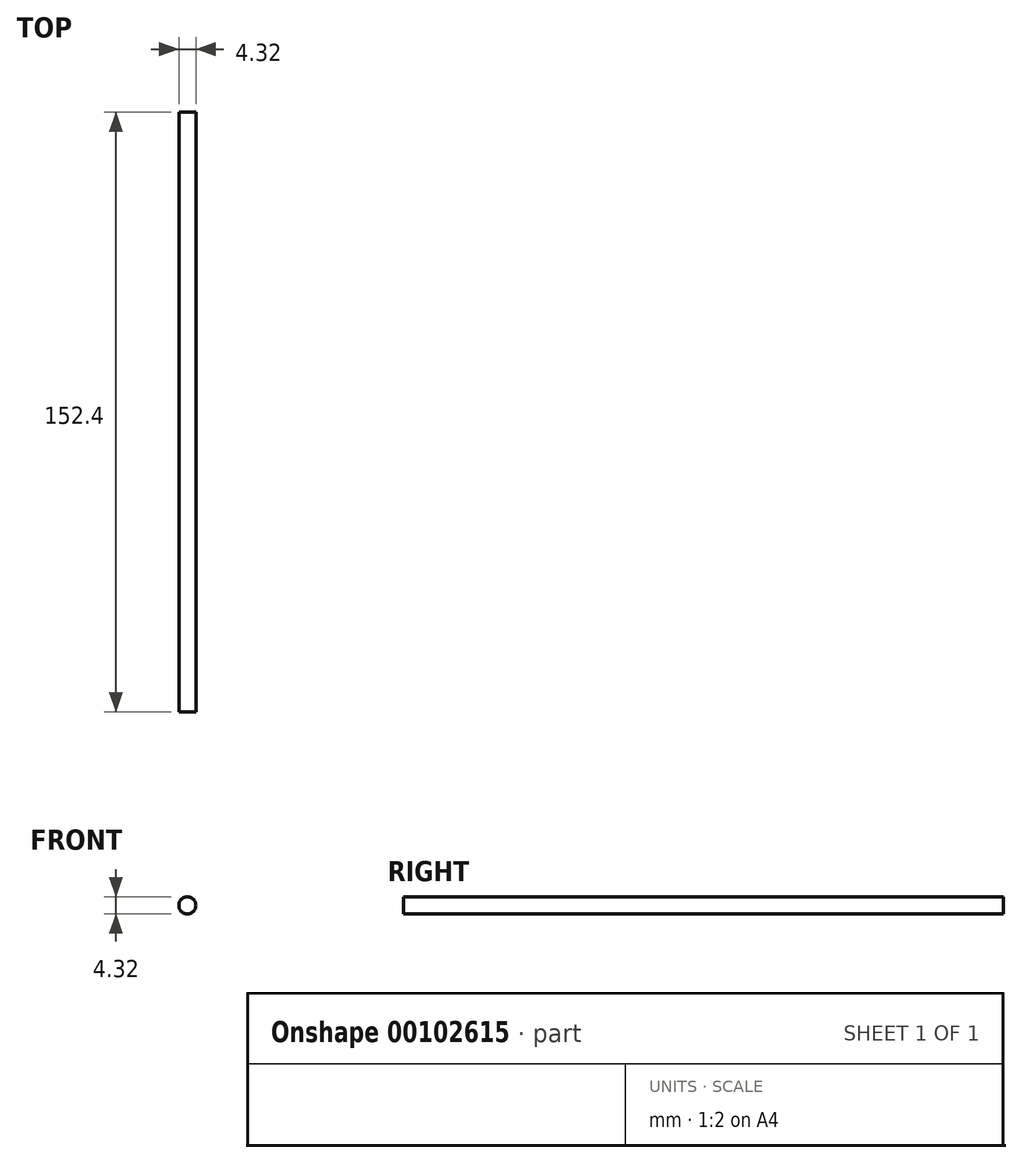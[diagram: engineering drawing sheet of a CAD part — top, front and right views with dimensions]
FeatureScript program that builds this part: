
annotation { "Feature Type Name" : "Feature", "Feature Type Description" : "" }
export const myFeature = defineFeature(function(context is Context, id is Id, definition is map)
    precondition{}
    {
        {
            var Q0;
            Q0=qCreatedBy(makeId("Front.planeOp"),FACE);
            var sketch = newSketch(context, id + "F0", { "sketchPlane" : qUnion([Q0])});
            skCircle(sketch, "E0", {"center": v(0, 0) * mm, "radius": 2.16 * mm});
            skSolve(sketch);
        }
        {
            var Q0;
            Q0=makeQuery(id+"F0.imprint","IMPRINT",FACE,{"disambiguationData":[TD([[makeQuery(id+"F0.imprint","IMPRINT",EDGE,{"derivedFrom":sQuery(id+"F0.wireOp",EDGE,"E0")}),1.0]])]});
            extrude(context, id + "F1", {"entities" : qUnion([Q0]), "depth" : 152.4 * mm});
        }
    });
